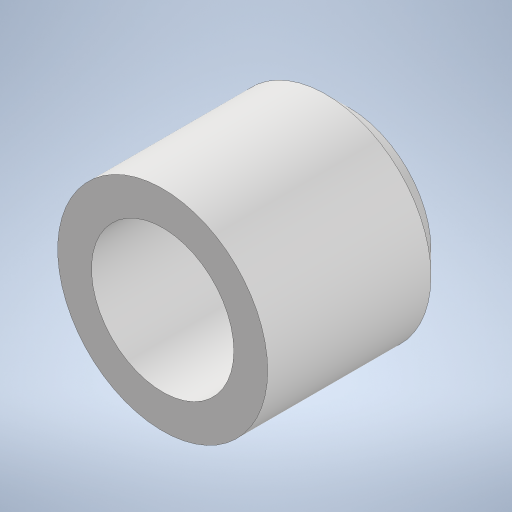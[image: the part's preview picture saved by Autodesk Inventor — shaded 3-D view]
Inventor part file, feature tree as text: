
AUTODESK INVENTOR PART (.ipt)
format: ipt  version: 2024.1 (Build 281209000, 209)  size: 241,152 bytes
history: native  units: in
note: dims shown in document units (in); Inventor stores cm internally (conversion verified against a paired STEP export)
features: extrude x3, sketch x3, chamfer x1, fillet x1
ambient origin geometry x8: Origin, YZ Plane, XZ Plane, XY Plane, X Axis, Y Axis, Z Axis, Center Point
bodies: Solid1 (feature_tree)
feature tree (8):
  extrude  "Extrusion1"  Depth=0.315in TaperAngle=0.0deg
  extrude  "Extrusion2"  Depth=0.2756in TaperAngle=0.0deg
  chamfer  "Chamfer1"  Distance=0.0394in Angle=45.0deg
  extrude  "Extrusion3"  TaperAngle=0.0deg  [1 undecoded]
  fillet  "Fillet1"  Radius=0.0197in
  sketch  "Sketch1"  dims[d0=0.3543in d1=0.315in d2=0.0in]
  sketch  "Sketch2"  dims[d3=0.2402in d4=0.2756in d5=0.0in d6=0.0394in d7=0.0787in d8=45.0deg]
  sketch  "Sketch3"  dims[d9=0.0197in d10=0.0in d11=0.0in d12=0.0197in]
note: 1 required parameter value undecoded (feature->parameter linkage not recoverable at this tier; creation-order binding heuristic only, values carry confidence <= 0.55)
